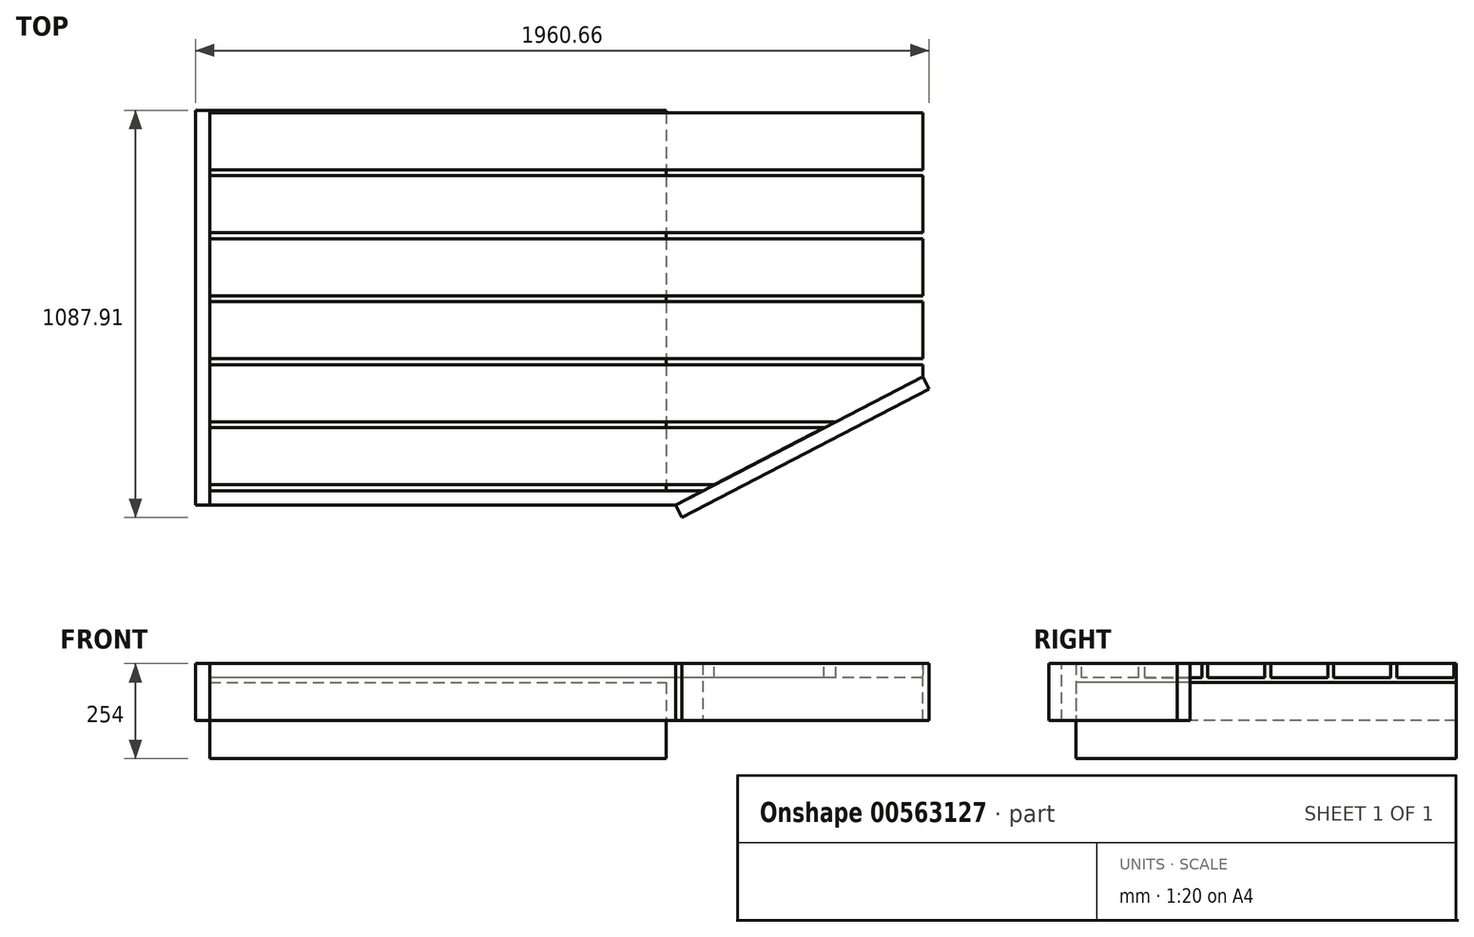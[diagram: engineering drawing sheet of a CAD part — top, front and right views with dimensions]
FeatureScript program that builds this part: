
annotation { "Feature Type Name" : "Feature", "Feature Type Description" : "" }
export const myFeature = defineFeature(function(context is Context, id is Id, definition is map)
    precondition{}
    {
        {
            var Q0;
            Q0=qCreatedBy(makeId("Top.planeOp"),FACE);
            var sketch = newSketch(context, id + "F0", { "sketchPlane" : qUnion([Q0])});
            skLineSegment(sketch, "E0.bottom", {"start": v(-609.6, 508) * mm, "end": v(609.6, 508) * mm});
            skLineSegment(sketch, "E0.top", {"start": v(-609.6, -508) * mm, "end": v(609.6, -508) * mm});
            skLineSegment(sketch, "E0.left", {"start": v(-609.6, 508) * mm, "end": v(-609.6, -508) * mm});
            skLineSegment(sketch, "E0.right", {"start": v(609.6, 508) * mm, "end": v(609.6, -508) * mm});
            skPoint(sketch, "E0.middle", {"position": v(0, 0) * mm});
            skLineSegment(sketch, "E1", {"start": v(609.6, 508) * mm, "end": v(1295.4, 508) * mm, "construction": true});
            skLineSegment(sketch, "E2", {"start": v(1295.4, 508) * mm, "end": v(1295.4, -203.2) * mm, "construction": true});
            skPoint(sketch, "E3.orphan", {"position": v(1295.4, 0) * mm});
            skSolve(sketch);
        }
        {
            var Q0;
            Q0 = qSketchRegion(id + "F0", true);
            extrude(context, id + "F1", {"entities" : qUnion([Q0]), "depth" : 203.2 * mm, "offsetDistance" : 25.4 * mm});
        }
        {
            var Q0;
            Q0=makeQuery(id+"F1.opExtrude","SWEPT_FACE",FACE,{"disambiguationData":[OSD([sQuery(id+"F0.wireOp",EDGE,"E0.left")])]});
            var sketch = newSketch(context, id + "F2", { "sketchPlane" : qUnion([Q0])});
            skLineSegment(sketch, "E4.bottom", {"start": v(508, 101.6) * mm, "end": v(546.1, 101.6) * mm});
            skLineSegment(sketch, "E4.top", {"start": v(508, 254) * mm, "end": v(546.1, 254) * mm});
            skLineSegment(sketch, "E4.left", {"start": v(508, 101.6) * mm, "end": v(508, 254) * mm});
            skLineSegment(sketch, "E4.right", {"start": v(546.1, 101.6) * mm, "end": v(546.1, 254) * mm});
            skLineSegment(sketch, "E5.bottom", {"start": v(492.12, 254) * mm, "end": v(339.72, 254) * mm});
            skLineSegment(sketch, "E5.top", {"start": v(492.12, 215.9) * mm, "end": v(339.72, 215.9) * mm});
            skLineSegment(sketch, "E5.left", {"start": v(492.12, 254) * mm, "end": v(492.12, 215.9) * mm});
            skLineSegment(sketch, "E5.right", {"start": v(339.72, 254) * mm, "end": v(339.72, 215.9) * mm});
            skPoint(sketch, "E5.middle", {"position": v(415.92, 234.95) * mm});
            skLineSegment(sketch, "E6.1.0.0", {"start": v(323.85, 254) * mm, "end": v(171.45, 254) * mm});
            skLineSegment(sketch, "E6.1.0.1", {"start": v(323.85, 215.9) * mm, "end": v(171.45, 215.9) * mm});
            skLineSegment(sketch, "E6.1.0.2", {"start": v(323.85, 254) * mm, "end": v(323.85, 215.9) * mm});
            skLineSegment(sketch, "E6.1.0.3", {"start": v(171.45, 254) * mm, "end": v(171.45, 215.9) * mm});
            skLineSegment(sketch, "E6.2.0.0", {"start": v(155.57, 254) * mm, "end": v(3.17, 254) * mm});
            skLineSegment(sketch, "E6.2.0.1", {"start": v(155.57, 215.9) * mm, "end": v(3.17, 215.9) * mm});
            skLineSegment(sketch, "E6.2.0.2", {"start": v(155.57, 254) * mm, "end": v(155.57, 215.9) * mm});
            skLineSegment(sketch, "E6.2.0.3", {"start": v(3.17, 254) * mm, "end": v(3.17, 215.9) * mm});
            skLineSegment(sketch, "E6.3.0.0", {"start": v(-12.7, 254) * mm, "end": v(-165.1, 254) * mm});
            skLineSegment(sketch, "E6.3.0.1", {"start": v(-12.7, 215.9) * mm, "end": v(-165.1, 215.9) * mm});
            skLineSegment(sketch, "E6.3.0.2", {"start": v(-12.7, 254) * mm, "end": v(-12.7, 215.9) * mm});
            skLineSegment(sketch, "E6.3.0.3", {"start": v(-165.1, 254) * mm, "end": v(-165.1, 215.9) * mm});
            skLineSegment(sketch, "E6.4.0.0", {"start": v(-180.98, 254) * mm, "end": v(-333.38, 254) * mm});
            skLineSegment(sketch, "E6.4.0.1", {"start": v(-180.98, 215.9) * mm, "end": v(-333.38, 215.9) * mm});
            skLineSegment(sketch, "E6.4.0.2", {"start": v(-180.98, 254) * mm, "end": v(-180.98, 215.9) * mm});
            skLineSegment(sketch, "E6.4.0.3", {"start": v(-333.38, 254) * mm, "end": v(-333.38, 215.9) * mm});
            skLineSegment(sketch, "E6.5.0.0", {"start": v(-349.25, 254) * mm, "end": v(-501.65, 254) * mm});
            skLineSegment(sketch, "E6.5.0.1", {"start": v(-349.25, 215.9) * mm, "end": v(-501.65, 215.9) * mm});
            skLineSegment(sketch, "E6.5.0.2", {"start": v(-349.25, 254) * mm, "end": v(-349.25, 215.9) * mm});
            skLineSegment(sketch, "E6.5.0.3", {"start": v(-501.65, 254) * mm, "end": v(-501.65, 215.9) * mm});
            skLineSegment(sketch, "E6.direction1", {"start": v(339.72, 254) * mm, "end": v(171.45, 254) * mm, "construction": true});
            skSolve(sketch);
        }
        {
            var Q0;
            Q0 = qSketchRegion(id + "F2", true);
            extrude(context, id + "F3", {"entities" : qUnion([Q0]), "oppositeDirection" : true, "depth" : 1905 * mm, "offsetDistance" : 25.4 * mm});
        }
        {
            var Q0;
            Q0=makeQuery(id+"F3.opExtrude","SWEPT_FACE",FACE,{"disambiguationData":[OSD([sQuery(id+"F2.wireOp",EDGE,"E4.right")])]});
            var sketch = newSketch(context, id + "F4", { "sketchPlane" : qUnion([Q0])});
            skLineSegment(sketch, "E7.bottom", {"start": v(-609.6, 254) * mm, "end": v(-647.7, 254) * mm});
            skLineSegment(sketch, "E7.top", {"start": v(-609.6, 101.6) * mm, "end": v(-647.7, 101.6) * mm});
            skLineSegment(sketch, "E7.left", {"start": v(-609.6, 254) * mm, "end": v(-609.6, 101.6) * mm});
            skLineSegment(sketch, "E7.right", {"start": v(-647.7, 254) * mm, "end": v(-647.7, 101.6) * mm});
            skSolve(sketch);
        }
        {
            var Q0;
            Q0 = qSketchRegion(id + "F4", true);
            extrude(context, id + "F5", {"entities" : qUnion([Q0]), "oppositeDirection" : true, "depth" : 1054.1 * mm, "offsetDistance" : 25.4 * mm});
        }
        {
            var Q0;
            Q0=makeQuery(id+"F3.opExtrude","SWEPT_FACE",FACE,{"disambiguationData":[OSD([sQuery(id+"F2.wireOp",EDGE,"E5.bottom")])]});
            var sketch = newSketch(context, id + "F6", { "sketchPlane" : qUnion([Q0])});
            skLineSegment(sketch, "E8", {"start": v(635, -546.1) * mm, "end": v(1295.4, -546.1) * mm});
            skLineSegment(sketch, "E9", {"start": v(1295.4, -546.1) * mm, "end": v(1295.4, -203.2) * mm});
            skLineSegment(sketch, "E10", {"start": v(1295.4, -203.2) * mm, "end": v(635, -546.1) * mm});
            skSolve(sketch);
        }
        {
            var Q0;
            Q0 = qSketchRegion(id + "F6", true);
            extrude(context, id + "F7", {"entities" : qUnion([Q0]), "operationType" : NewBodyOperationType.REMOVE, "endBound" : BoundingType.THROUGH_ALL, "oppositeDirection" : true, "depth" : 25.4 * mm, "offsetDistance" : 25.4 * mm});
        }
        {
            var Q0;
            Q0=makeQuery(id+"F3.opExtrude","SWEPT_FACE",FACE,{"disambiguationData":[OSD([sQuery(id+"F2.wireOp",EDGE,"E6.1.0.0")])]});
            var sketch = newSketch(context, id + "F8", { "sketchPlane" : qUnion([Q0])});
            skLineSegment(sketch, "E11", {"start": v(635, -546.1) * mm, "end": v(1295.4, -203.2) * mm});
            skLineSegment(sketch, "E12", {"start": v(1295.4, -203.2) * mm, "end": v(1312.96, -237.01) * mm});
            skLineSegment(sketch, "E13", {"start": v(1312.96, -237.01) * mm, "end": v(652.56, -579.91) * mm});
            skLineSegment(sketch, "E14", {"start": v(652.56, -579.91) * mm, "end": v(635, -546.1) * mm});
            skSolve(sketch);
        }
        {
            var Q0;
            Q0 = qSketchRegion(id + "F8", true);
            extrude(context, id + "F9", {"entities" : qUnion([Q0]), "oppositeDirection" : true, "depth" : 152.4 * mm, "offsetDistance" : 25.4 * mm});
        }
    });
